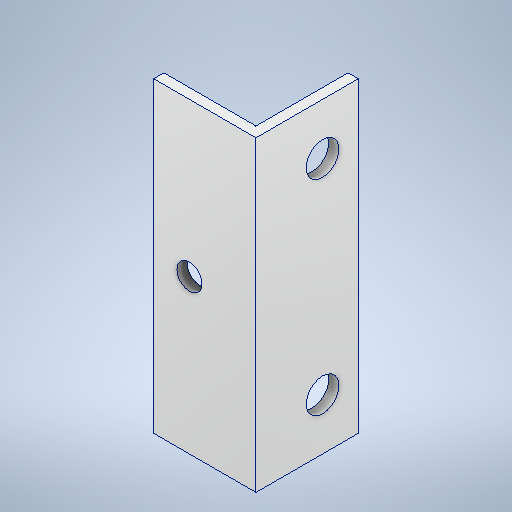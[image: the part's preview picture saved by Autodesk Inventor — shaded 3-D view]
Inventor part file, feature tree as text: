
AUTODESK INVENTOR PART (.ipt)
format: ipt  version: 2025 (Build 290162000, 162)  size: 264,704 bytes
history: native  units: mm
features: sketch x3, hole x2, other x1, extrude x1, projected_geometry x1
ambient origin geometry x8: Origin, YZ Plane, XZ Plane, XY Plane, X Axis, Y Axis, Z Axis, Center Point
bodies: Body1 (feature_tree)
feature tree (8):
  other  "Těleso1"
  extrude  "Vysunutí1"  Depth=10.0mm
  hole  "Díra1"  [1 undecoded]
  hole  "Díra2"  [1 undecoded]
  sketch  "Náčrt1"
  sketch  "Náčrt2"
  sketch  "Náčrt3"
  projected_geometry  "Promítnutá smyčka1"
note: 2 required parameter values undecoded (feature->parameter linkage not recoverable at this tier; creation-order binding heuristic only, values carry confidence <= 0.55)
